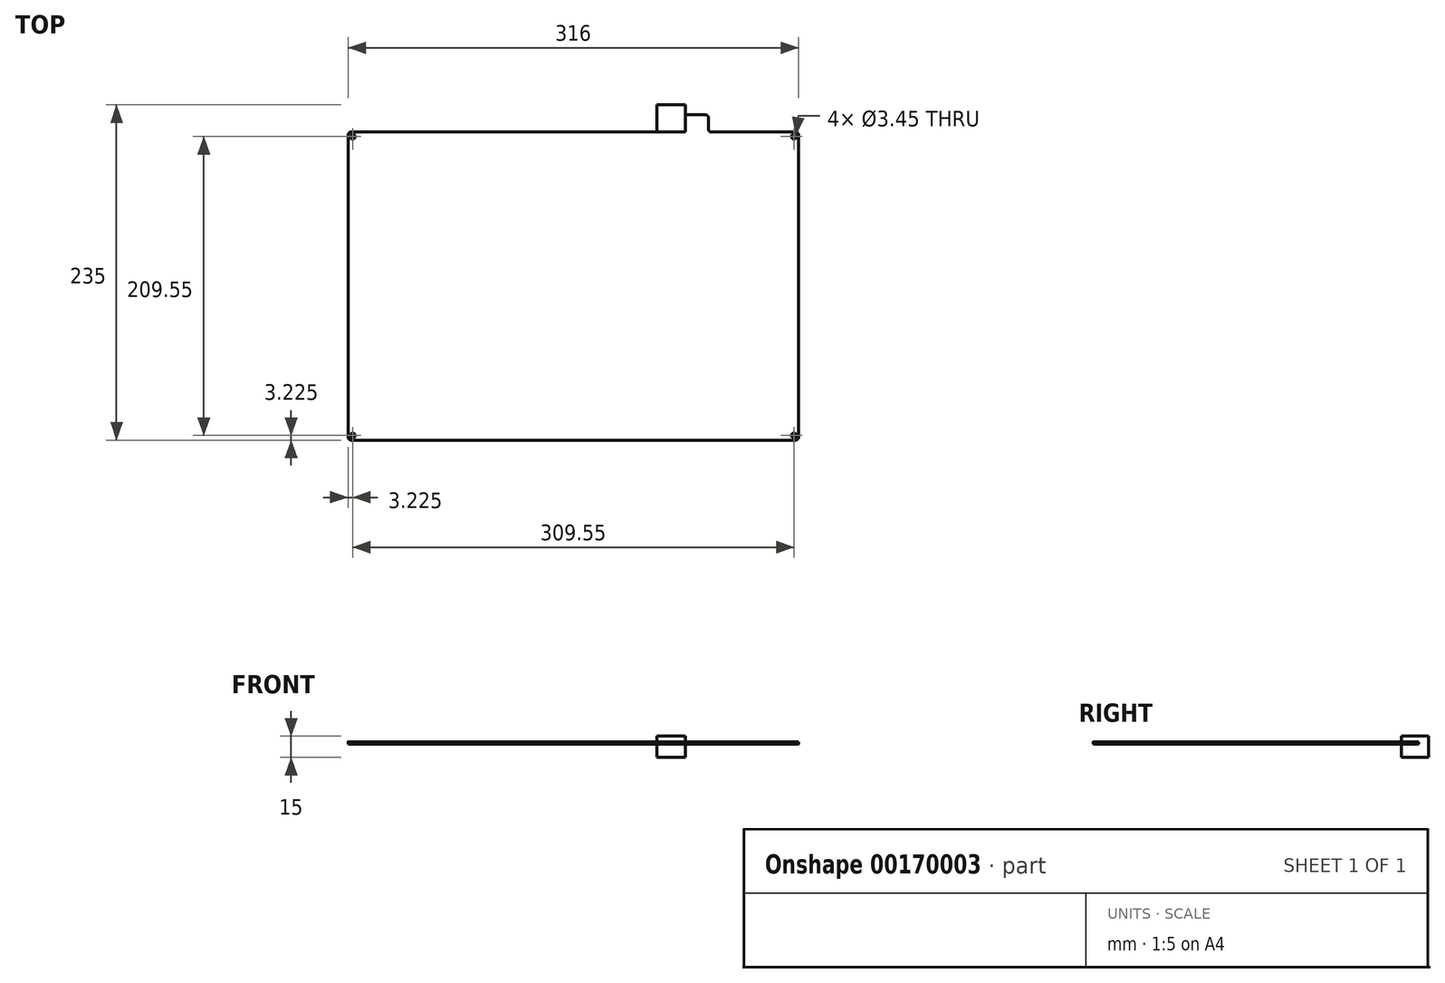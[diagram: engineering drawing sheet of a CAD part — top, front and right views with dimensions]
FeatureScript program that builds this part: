
annotation { "Feature Type Name" : "Feature", "Feature Type Description" : "" }
export const myFeature = defineFeature(function(context is Context, id is Id, definition is map)
    precondition{}
    {
        {
            var Q0;
            Q0=qCreatedBy(makeId("Top.planeOp"),FACE);
            var sketch = newSketch(context, id + "F0", { "sketchPlane" : qUnion([Q0])});
            skLineSegment(sketch, "E0.bottom", {"start": v(156, 108) * mm, "end": v(96.75, 108) * mm});
            skLineSegment(sketch, "E0.top", {"start": v(156, -108) * mm, "end": v(-156, -108) * mm});
            skLineSegment(sketch, "E0.left", {"start": v(158, 106) * mm, "end": v(158, -106) * mm});
            skLineSegment(sketch, "E0.right", {"start": v(-158, 106) * mm, "end": v(-158, -106) * mm});
            skPoint(sketch, "E0.middle", {"position": v(0, 0) * mm});
            skLineSegment(sketch, "E1.bottom", {"start": v(58.5, 120) * mm, "end": v(92.75, 120) * mm});
            skLineSegment(sketch, "E1.left", {"start": v(58.5, 120) * mm, "end": v(58.5, 108) * mm});
            skLineSegment(sketch, "E1.right", {"start": v(94.75, 118) * mm, "end": v(94.75, 110) * mm});
            skPoint(sketch, "E2.visualSharp", {"position": v(94.75, 120) * mm});
            skArc(sketch, "E2.filletArc", {"start": v(94.75, 118) * mm, "mid": v(94.16, 119.41) * mm, "end": v(92.75, 120) * mm});
            skLineSegment(sketch, "E3.trimOffspring", {"start": v(58.5, 108) * mm, "end": v(-156, 108) * mm});
            skPoint(sketch, "E4.visualSharp", {"position": v(94.75, 108) * mm});
            skArc(sketch, "E4.filletArc", {"start": v(94.75, 110) * mm, "mid": v(95.34, 108.59) * mm, "end": v(96.75, 108) * mm});
            skPoint(sketch, "E5.visualSharp", {"position": v(158, 108) * mm});
            skArc(sketch, "E5.filletArc", {"start": v(158, 106) * mm, "mid": v(157.41, 107.41) * mm, "end": v(156, 108) * mm});
            skPoint(sketch, "E6.visualSharp", {"position": v(158, -108) * mm});
            skArc(sketch, "E6.filletArc", {"start": v(156, -108) * mm, "mid": v(157.41, -107.41) * mm, "end": v(158, -106) * mm});
            skPoint(sketch, "E7.visualSharp", {"position": v(-158, -108) * mm});
            skArc(sketch, "E7.filletArc", {"start": v(-158, -106) * mm, "mid": v(-157.41, -107.41) * mm, "end": v(-156, -108) * mm});
            skPoint(sketch, "E8.visualSharp", {"position": v(-158, 108) * mm});
            skArc(sketch, "E8.filletArc", {"start": v(-156, 108) * mm, "mid": v(-157.41, 107.41) * mm, "end": v(-158, 106) * mm});
            skCircle(sketch, "E9", {"center": v(154.78, 104.77) * mm, "radius": 1.73 * mm});
            skCircle(sketch, "E10.MirrorC", {"center": v(154.78, -104.77) * mm, "radius": 1.73 * mm});
            skCircle(sketch, "E11.MirrorC", {"center": v(-154.78, 104.77) * mm, "radius": 1.73 * mm});
            skCircle(sketch, "E12.MirrorC", {"center": v(-154.78, -104.77) * mm, "radius": 1.73 * mm});
            skSolve(sketch);
        }
        {
            var Q0;
            Q0=makeQuery(id+"F0.imprint","IMPRINT",FACE,{"disambiguationData":[TD([[makeQuery(id+"F0.imprint","IMPRINT",EDGE,{"derivedFrom":sQuery(id+"F0.wireOp",EDGE,"E0.bottom")}),1.0]])]});
            extrude(context, id + "F1", {"entities" : qUnion([Q0]), "depth" : 1.6 * mm});
        }
        {
            var Q0;
            Q0=makeQuery(id+"F1.opExtrude","SWEPT_FACE",FACE,{"disambiguationData":[OSD([sQuery(id+"F0.wireOp",EDGE,"E3.trimOffspring")])]});
            var sketch = newSketch(context, id + "F2", { "sketchPlane" : qUnion([Q0])});
            skLineSegment(sketch, "E13.bottom", {"start": v(-58.5, 5.6) * mm, "end": v(-78.5, 5.6) * mm});
            skLineSegment(sketch, "E13.top", {"start": v(-58.5, -9.4) * mm, "end": v(-78.5, -9.4) * mm});
            skLineSegment(sketch, "E13.left", {"start": v(-58.5, 5.6) * mm, "end": v(-58.5, -9.4) * mm});
            skLineSegment(sketch, "E13.right", {"start": v(-78.5, 5.6) * mm, "end": v(-78.5, -9.4) * mm});
            skSolve(sketch);
        }
        {
            var Q0;
            {var subQ4=sQuery(id+"F2.wireOp",EDGE,"E13.bottom");Q0=makeQuery(id+"F2.imprint","IMPRINT",FACE,{"disambiguationData":[TD([[makeQuery(id+"F2.imprint","IMPRINT",EDGE,{"derivedFrom":subQ4}),1.0]])]});}
            extrude(context, id + "F3", {"entities" : qUnion([Q0]), "operationType" : NewBodyOperationType.ADD, "depth" : 19 * mm});
        }
    });
